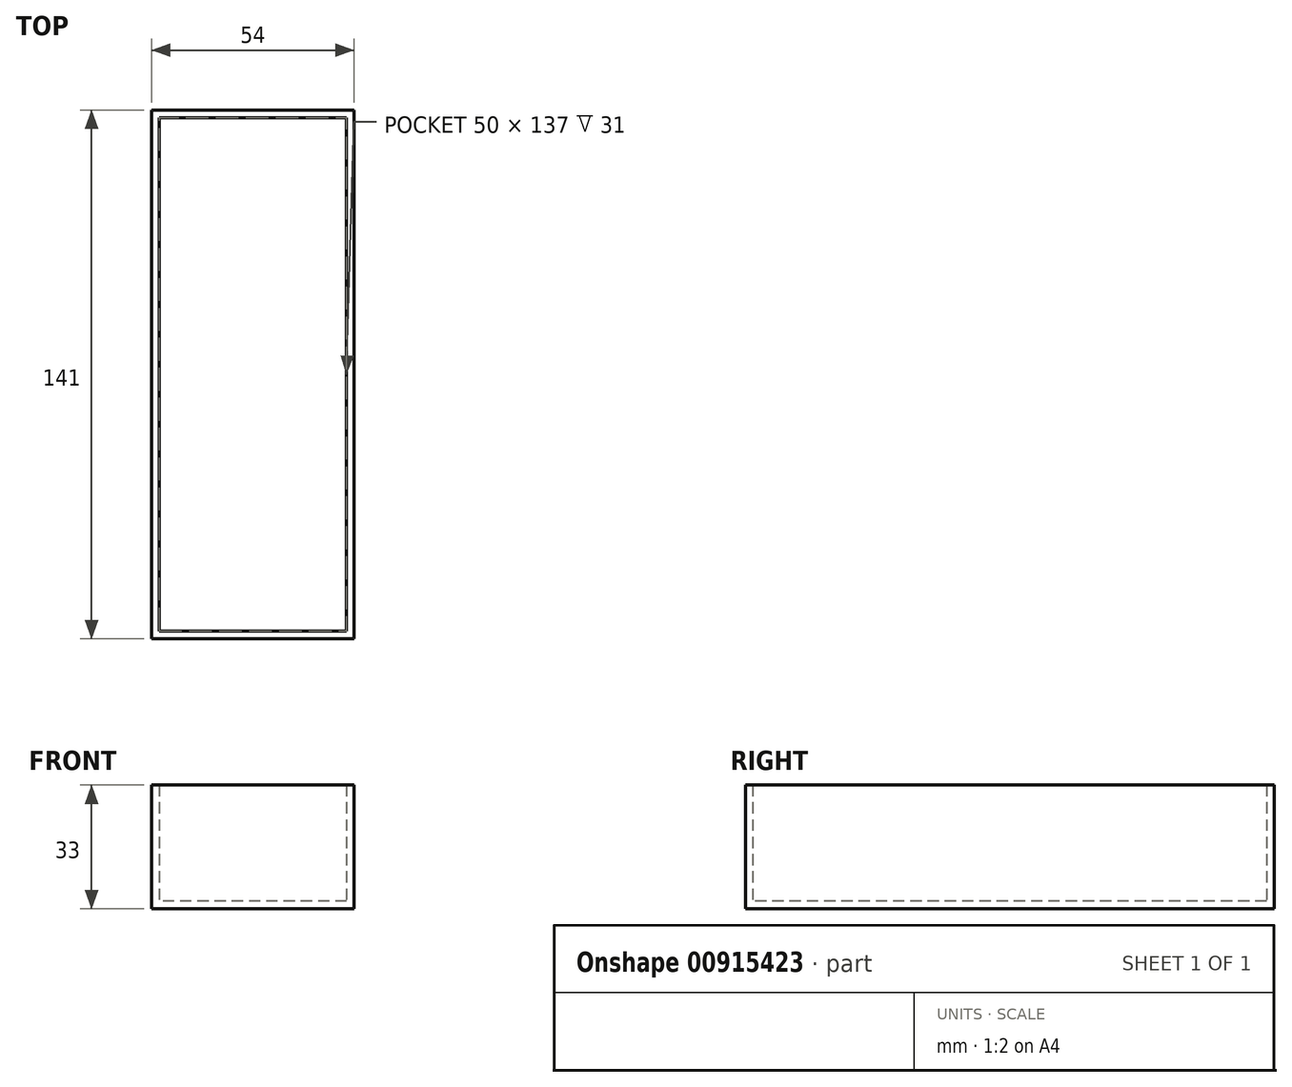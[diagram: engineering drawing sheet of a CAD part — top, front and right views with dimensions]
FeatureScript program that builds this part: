
annotation { "Feature Type Name" : "Feature", "Feature Type Description" : "" }
export const myFeature = defineFeature(function(context is Context, id is Id, definition is map)
    precondition{}
    {
        {
            var Q0;
            Q0=qCreatedBy(makeId("Top.planeOp"),FACE);
            var sketch = newSketch(context, id + "F0", { "sketchPlane" : qUnion([Q0])});
            skLineSegment(sketch, "E0.bottom", {"start": v(0, 0) * mm, "end": v(54, 0) * mm});
            skLineSegment(sketch, "E0.top", {"start": v(0, 141) * mm, "end": v(54, 141) * mm});
            skLineSegment(sketch, "E0.left", {"start": v(0, 0) * mm, "end": v(0, 141) * mm});
            skLineSegment(sketch, "E0.right", {"start": v(54, 0) * mm, "end": v(54, 141) * mm});
            skLineSegment(sketch, "E1.bottom", {"start": v(2, 2) * mm, "end": v(52, 2) * mm});
            skLineSegment(sketch, "E1.top", {"start": v(2, 139) * mm, "end": v(52, 139) * mm});
            skLineSegment(sketch, "E1.left", {"start": v(2, 2) * mm, "end": v(2, 139) * mm});
            skLineSegment(sketch, "E1.right", {"start": v(52, 2) * mm, "end": v(52, 139) * mm});
            skSolve(sketch);
        }
        {
            var Q0;
            Q0 = qSketchRegion(id + "F0", true);
            extrude(context, id + "F1", {"entities" : qUnion([Q0]), "depth" : 33 * mm, "offsetDistance" : 25 * mm});
        }
        {
            var Q0;
            Q0=makeQuery(id+"F1.opExtrude","SWEPT_FACE",FACE,{"disambiguationData":[OSD([sQuery(id+"F0.wireOp",EDGE,"E0.bottom")])]});
            var sketch = newSketch(context, id + "F2", { "sketchPlane" : qUnion([Q0])});
            skLineSegment(sketch, "E2.bottom", {"start": v(0, 0) * mm, "end": v(54, 0) * mm});
            skLineSegment(sketch, "E2.top", {"start": v(0, 2) * mm, "end": v(54, 2) * mm});
            skLineSegment(sketch, "E2.left", {"start": v(0, 0) * mm, "end": v(0, 2) * mm});
            skLineSegment(sketch, "E2.right", {"start": v(54, 0) * mm, "end": v(54, 2) * mm});
            skSolve(sketch);
        }
        {
            var Q0;
            Q0 = qSketchRegion(id + "F2", true);
            extrude(context, id + "F3", {"entities" : qUnion([Q0]), "operationType" : NewBodyOperationType.ADD, "oppositeDirection" : true, "depth" : 141 * mm, "offsetDistance" : 25 * mm});
        }
        {
            var Q0;
            Q0=makeQuery(id+"F1.opExtrude","SWEPT_FACE",FACE,{"disambiguationData":[OSD([sQuery(id+"F0.wireOp",EDGE,"E0.bottom")])]});
            var sketch = newSketch(context, id + "F4", { "sketchPlane" : qUnion([Q0])});
            skLineSegment(sketch, "E3", {"start": v(0, 33) * mm, "end": v(0, 0) * mm});
            skSolve(sketch);
        }
        {
            var Q0;
            Q0=sQuery(id+"F4.wireOp",EDGE,"E3");
            extrude(context, id + "F5", {"bodyType" : ToolBodyType.SURFACE, "surfaceEntities" : qUnion([Q0]), "oppositeDirection" : true, "depth" : 141 * mm, "offsetDistance" : 25 * mm});
        }
        {
            var Q0;
            Q0=makeQuery(id+"F1.opExtrude","SWEPT_FACE",FACE,{"disambiguationData":[OSD([sQuery(id+"F0.wireOp",EDGE,"E0.bottom")])]});
            var sketch = newSketch(context, id + "F6", { "sketchPlane" : qUnion([Q0])});
            skLineSegment(sketch, "E4", {"start": v(54, 0) * mm, "end": v(54, 33) * mm});
            skSolve(sketch);
        }
        {
            var Q0;
            Q0=sQuery(id+"F6.wireOp",EDGE,"E4");
            extrude(context, id + "F7", {"bodyType" : ToolBodyType.SURFACE, "surfaceEntities" : qUnion([Q0]), "oppositeDirection" : true, "depth" : 141 * mm, "offsetDistance" : 25 * mm});
        }
        {
            var Q0;
            Q0=makeQuery(id+"F1.opExtrude","SWEPT_FACE",FACE,{"disambiguationData":[OSD([sQuery(id+"F0.wireOp",EDGE,"E0.bottom")])]});
            var sketch = newSketch(context, id + "F8", { "sketchPlane" : qUnion([Q0])});
            skLineSegment(sketch, "E5", {"start": v(0, 0) * mm, "end": v(54, 0) * mm});
            skSolve(sketch);
        }
        {
            var Q0;
            Q0=sQuery(id+"F8.wireOp",EDGE,"E5");
            extrude(context, id + "F9", {"bodyType" : ToolBodyType.SURFACE, "surfaceEntities" : qUnion([Q0]), "oppositeDirection" : true, "depth" : 141 * mm, "offsetDistance" : 25 * mm});
        }
        {
            var Q0;
            Q0=makeQuery(id+"F9.opExtrude","SWEPT_FACE",FACE,{"disambiguationData":[OSD([sQuery(id+"F8.wireOp",EDGE,"E5")])]});
            var sketch = newSketch(context, id + "F10", { "sketchPlane" : qUnion([Q0])});
            skLineSegment(sketch, "E6", {"start": v(0, 0) * mm, "end": v(54, 0) * mm});
            skSolve(sketch);
        }
        {
            var Q0;
            Q0=sQuery(id+"F10.wireOp",EDGE,"E6");
            extrude(context, id + "F11", {"bodyType" : ToolBodyType.SURFACE, "surfaceEntities" : qUnion([Q0]), "depth" : 33 * mm, "offsetDistance" : 25 * mm});
        }
        {
            var Q0;
            Q0=makeQuery(id+"F9.opExtrude","SWEPT_FACE",FACE,{"disambiguationData":[OSD([sQuery(id+"F8.wireOp",EDGE,"E5")])]});
            var sketch = newSketch(context, id + "F12", { "sketchPlane" : qUnion([Q0])});
            skLineSegment(sketch, "E7", {"start": v(54, 141) * mm, "end": v(0, 141) * mm});
            skSolve(sketch);
        }
        {
            var Q0;
            Q0=sQuery(id+"F12.wireOp",EDGE,"E7");
            extrude(context, id + "F13", {"bodyType" : ToolBodyType.SURFACE, "surfaceEntities" : qUnion([Q0]), "depth" : 33 * mm, "offsetDistance" : 25 * mm});
        }
    });
